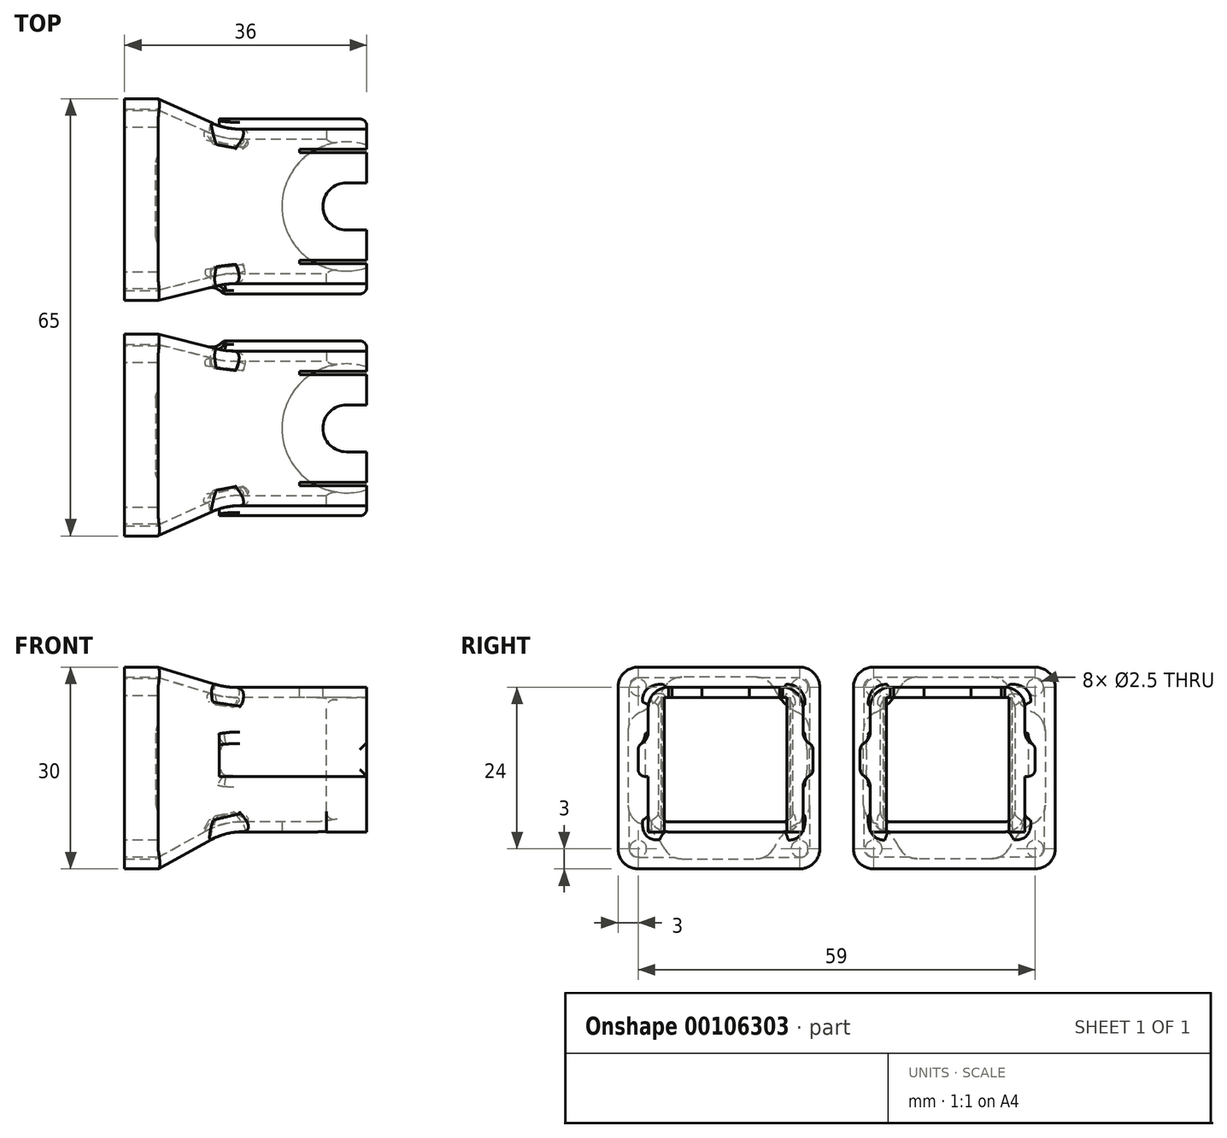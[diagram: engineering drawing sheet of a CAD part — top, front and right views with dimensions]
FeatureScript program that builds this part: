
annotation { "Feature Type Name" : "Feature", "Feature Type Description" : "" }
export const myFeature = defineFeature(function(context is Context, id is Id, definition is map)
    precondition{}
    {
        {
            var Q0;
            Q0=qCreatedBy(makeId("Front.planeOp"),FACE);
            var sketch = newSketch(context, id + "F0", { "sketchPlane" : qUnion([Q0])});
            skLineSegment(sketch, "E0.bottom", {"start": v(10.5, -10.75) * mm, "end": v(-10.5, -10.75) * mm});
            skLineSegment(sketch, "E0.top", {"start": v(10.5, 10.75) * mm, "end": v(-10.5, 10.75) * mm});
            skLineSegment(sketch, "E0.left", {"start": v(10.5, -10.75) * mm, "end": v(10.5, 10.75) * mm});
            skLineSegment(sketch, "E0.right", {"start": v(-10.5, -10.75) * mm, "end": v(-10.5, 10.75) * mm});
            skPoint(sketch, "E0.middle", {"position": v(0, 0) * mm});
            skSolve(sketch);
        }
        {
            var Q0;
            Q0=qSketchRegion(id+"F0",true);
            extrude(context, id + "F1", {"entities" : qUnion([Q0]), "endBound" : BoundingType.SYMMETRIC, "depth" : 23 * mm});
        }
        {
            var Q0;
            Q0=makeQuery(id+"F1.opExtrude","SWEPT_FACE",FACE,{"disambiguationData":[OSD([sQuery(id+"F0.wireOp",EDGE,"E0.right")])]});
            cPlane(context, id + "F2", {"entities" : qUnion([Q0]), "cplaneType" : CPlaneType.OFFSET, "offset" : 10 * mm, "width" : 150 * mm, "height" : 150 * mm});
        }
        {
            var Q0;
            Q0=qCreatedBy(id+"F2.planeOp",FACE);
            var sketch = newSketch(context, id + "F3", { "sketchPlane" : qUnion([Q0])});
            skLineSegment(sketch, "E1.bottom", {"start": v(14, -16.25) * mm, "end": v(-16, -16.25) * mm});
            skLineSegment(sketch, "E1.top", {"start": v(14, 13.75) * mm, "end": v(-16, 13.75) * mm});
            skLineSegment(sketch, "E1.left", {"start": v(14, -16.25) * mm, "end": v(14, 13.75) * mm});
            skLineSegment(sketch, "E1.right", {"start": v(-16, -16.25) * mm, "end": v(-16, 13.75) * mm});
            skPoint(sketch, "E1.middle", {"position": v(-1, -1.25) * mm});
            skSolve(sketch);
        }
        {
            var Q1;
            Q1=makeQuery(id+"F1.opExtrude","SWEPT_FACE",FACE,{"disambiguationData":[OSD([sQuery(id+"F0.wireOp",EDGE,"E0.right")])]});
            var Q2;
            Q2=makeQuery(id+"F3.imprint","IMPRINT",FACE,{"disambiguationData":[TD([[makeQuery(id+"F3.imprint","IMPRINT",EDGE,{"derivedFrom":sQuery(id+"F3.wireOp",EDGE,"E1.bottom")}),-1.0]])]});
            loft(context, id + "F4", {"operationType" : NewBodyOperationType.ADD, "sheetProfilesArray" : [{ "sheetProfileEntities" : qUnion([Q1]) }, { "sheetProfileEntities" : qUnion([Q2]) }]});
        }
        {
            var Q0;
            Q0=makeQuery(id+"F4.opLoft","CAP_FACE",FACE,{"disambiguationData":[OSD([makeQuery(id+"F3.imprint","IMPRINT",FACE,{"disambiguationData":[TD([[makeQuery(id+"F3.imprint","IMPRINT",EDGE,{"derivedFrom":sQuery(id+"F3.wireOp",EDGE,"E1.bottom")}),-1.0]])]})])],"isStart":true});
            var sketch = newSketch(context, id + "F5", { "sketchPlane" : qUnion([Q0])});
            skLineSegment(sketch, "E2.bottom", {"start": v(-16, 13.75) * mm, "end": v(14, 13.75) * mm});
            skLineSegment(sketch, "E2.top", {"start": v(-16, -16.25) * mm, "end": v(14, -16.25) * mm});
            skLineSegment(sketch, "E2.left", {"start": v(-16, 13.75) * mm, "end": v(-16, -16.25) * mm});
            skLineSegment(sketch, "E2.right", {"start": v(14, 13.75) * mm, "end": v(14, -16.25) * mm});
            skSolve(sketch);
        }
        {
            var Q0;
            Q0=qSketchRegion(id+"F5",true);
            extrude(context, id + "F6", {"entities" : qUnion([Q0]), "operationType" : NewBodyOperationType.ADD, "depth" : 5 * mm});
        }
        {
            var Q0;
            {var subQ1=sQuery(id+"F0.wireOp",EDGE,"E0.left");var subQ2=sQuery(id+"F0.wireOp",EDGE,"E0.top");Q0=makeQuery(id+"Fz8CBDRqYWuNpRD_1.boolean.opBoolean","SPLIT",EDGE,{"disambiguationData":[TD([makeQuery(id+"F1.opExtrude","SWEPT_FACE",FACE,{"disambiguationData":[OSD([subQ1])]})])],"derivedFrom":makeQuery(id+"F1.opExtrude","CAP_EDGE",EDGE,{"disambiguationData":[OSD([subQ2])],"isStart":false})});}
            var Q1;
            Q1=makeQuery(id+"F1.opExtrude","CAP_EDGE",EDGE,{"disambiguationData":[OSD([sQuery(id+"F0.wireOp",EDGE,"E0.bottom")])],"isStart":false});
            var Q2;
            {var subQ0=sQuery(id+"F0.wireOp",EDGE,"E0.left");var subQ1=sQuery(id+"F0.wireOp",EDGE,"E0.top");Q2=makeQuery(id+"Fz8CBDRqYWuNpRD_1.boolean.opBoolean","SPLIT",EDGE,{"disambiguationData":[TD([makeQuery(id+"F1.opExtrude","SWEPT_FACE",FACE,{"disambiguationData":[OSD([subQ0])]})])],"derivedFrom":makeQuery(id+"F1.opExtrude","CAP_EDGE",EDGE,{"disambiguationData":[OSD([subQ1])],"isStart":true})});}
            var Q3;
            Q3=makeQuery(id+"F1.opExtrude","CAP_EDGE",EDGE,{"disambiguationData":[OSD([sQuery(id+"F0.wireOp",EDGE,"E0.bottom")])],"isStart":true});
            var Q4;
            Q4=makeQuery(id+"F4.opLoft","SWEPT_EDGE",EDGE,{"disambiguationData":[OSD([sQuery(id+"F0.wireOp",EDGE,"E0.bottom"),sQuery(id+"F0.wireOp",EDGE,"E0.right"),sQuery(id+"F3.wireOp",EDGE,"E1.bottom"),sQuery(id+"F3.wireOp",EDGE,"E1.right")])]});
            var Q5;
            Q5=makeQuery(id+"F4.opLoft","SWEPT_EDGE",EDGE,{"disambiguationData":[OSD([sQuery(id+"F0.wireOp",EDGE,"E0.bottom"),sQuery(id+"F0.wireOp",EDGE,"E0.right"),sQuery(id+"F3.wireOp",EDGE,"E1.bottom"),sQuery(id+"F3.wireOp",EDGE,"E1.left")])]});
            var Q6;
            Q6=makeQuery(id+"F4.opLoft","SWEPT_EDGE",EDGE,{"disambiguationData":[OSD([sQuery(id+"F0.wireOp",EDGE,"E0.top"),sQuery(id+"F0.wireOp",EDGE,"E0.right"),sQuery(id+"F3.wireOp",EDGE,"E1.top"),sQuery(id+"F3.wireOp",EDGE,"E1.left")])]});
            var Q7;
            Q7=makeQuery(id+"F4.opLoft","SWEPT_EDGE",EDGE,{"disambiguationData":[OSD([sQuery(id+"F0.wireOp",EDGE,"E0.top"),sQuery(id+"F0.wireOp",EDGE,"E0.right"),sQuery(id+"F3.wireOp",EDGE,"E1.top"),sQuery(id+"F3.wireOp",EDGE,"E1.right")])]});
            var Q8;
            {var subQ1=sQuery(id+"F0.wireOp",EDGE,"E0.right");var subQ2=sQuery(id+"F0.wireOp",EDGE,"E0.top");Q8=makeQuery(id+"Fz8CBDRqYWuNpRD_1.boolean.opBoolean","SPLIT",EDGE,{"disambiguationData":[TD([makeQuery(id+"F1.opExtrude","SWEPT_FACE",FACE,{"disambiguationData":[OSD([subQ1])]})])],"derivedFrom":makeQuery(id+"F1.opExtrude","CAP_EDGE",EDGE,{"disambiguationData":[OSD([subQ2])],"isStart":false})});}
            var Q9;
            {var subQ1=sQuery(id+"F0.wireOp",EDGE,"E0.right");var subQ2=sQuery(id+"F0.wireOp",EDGE,"E0.top");Q9=makeQuery(id+"Fz8CBDRqYWuNpRD_1.boolean.opBoolean","SPLIT",EDGE,{"disambiguationData":[TD([makeQuery(id+"F1.opExtrude","SWEPT_FACE",FACE,{"disambiguationData":[OSD([subQ1])]})])],"derivedFrom":makeQuery(id+"F1.opExtrude","CAP_EDGE",EDGE,{"disambiguationData":[OSD([subQ2])],"isStart":true})});}
            fillet(context, id + "F7", {"entities" : qUnion([Q0, Q1, Q2, Q3, Q4, Q5, Q6, Q7, Q8, Q9]), "radius" : 3 * mm, "tangentPropagation" : true, "allowEdgeOverflow" : false});
        }
        {
            var Q0;
            {var subQ0=sQuery(id+"F0.wireOp",EDGE,"E0.right");var subQ1=sQuery(id+"F0.wireOp",EDGE,"E0.top");Q0=makeQuery(id+"F4.boolean.opBoolean","MERGE",EDGE,{"derivedFrom":[makeQuery(id+"F1.opExtrude","SWEPT_EDGE",EDGE,{"disambiguationData":[OSD([subQ1,subQ0])]}),makeQuery(id+"F4.opLoft","MID_CAP_EDGE",EDGE,{"disambiguationData":[OSD([subQ1,subQ0])],"capPos":0.0})]});}
            fillet(context, id + "F8", {"entities" : qUnion([Q0]), "radius" : 10 * mm, "tangentPropagation" : true, "allowEdgeOverflow" : false});
        }
        {
            var Q0;
            Q0=makeQuery(id+"F6.opExtrude","CAP_FACE",FACE,{"disambiguationData":[OSD([sQuery(id+"F5.wireOp",EDGE,"E2.bottom"),sQuery(id+"F5.wireOp",EDGE,"E2.top"),sQuery(id+"F5.wireOp",EDGE,"E2.left"),sQuery(id+"F5.wireOp",EDGE,"E2.right")])],"isStart":false});
            var Q1;
            Q1=makeQuery(id+"F7RU65wIXhI5Ua7_1.boolean.opBoolean","COPY",FACE,{"derivedFrom":makeQuery(id+"F7RU65wIXhI5Ua7_1.opExtrude","SWEPT_FACE",FACE,{"disambiguationData":[OSD([sQuery(id+"F3H2WqU3KsAX9Bc_1.wireOp",EDGE,"QCEsvqZN-Nejr-OE69-qjgT-Q3P4DVGDmgon")])]})});
            var Q2;
            Q2=makeQuery(id+"F1.opExtrude","SWEPT_FACE",FACE,{"disambiguationData":[OSD([sQuery(id+"F0.wireOp",EDGE,"E0.left")])]});
            shell(context, id + "F9", {"entities" : qUnion([Q0, Q1, Q2]), "thickness" : 1.5 * mm});
        }
        {
            var Q0;
            Q0=makeQuery(id+"F1.opExtrude","SWEPT_FACE",FACE,{"disambiguationData":[OSD([sQuery(id+"F0.wireOp",EDGE,"E0.top")])]});
            var sketch = newSketch(context, id + "F10", { "sketchPlane" : qUnion([Q0])});
            skLineSegment(sketch, "E3.bottom", {"start": v(4.5, 11.5) * mm, "end": v(10.5, 11.5) * mm});
            skLineSegment(sketch, "E3.top", {"start": v(4.5, 8.5) * mm, "end": v(10.5, 8.5) * mm});
            skLineSegment(sketch, "E3.left", {"start": v(4.5, 11.5) * mm, "end": v(4.5, 8.5) * mm});
            skLineSegment(sketch, "E3.right", {"start": v(10.5, 11.5) * mm, "end": v(10.5, 8.5) * mm});
            skLineSegment(sketch, "E4.MirrorCS", {"start": v(4.5, -11.5) * mm, "end": v(10.5, -11.5) * mm});
            skLineSegment(sketch, "E5.MirrorCS", {"start": v(10.5, -11.5) * mm, "end": v(10.5, -8.5) * mm});
            skLineSegment(sketch, "E6.MirrorCS", {"start": v(4.5, -11.5) * mm, "end": v(4.5, -8.5) * mm});
            skLineSegment(sketch, "E7.MirrorCS", {"start": v(4.5, -8.5) * mm, "end": v(10.5, -8.5) * mm});
            skSolve(sketch);
        }
        {
            var Q0;
            Q0=qSketchRegion(id+"F10",true);
            var Q1;
            Q1=makeQuery(id+"F1.opExtrude","SWEPT_FACE",FACE,{"disambiguationData":[OSD([sQuery(id+"F0.wireOp",EDGE,"E0.bottom")])]});
            extrude(context, id + "F11", {"entities" : qUnion([Q0]), "operationType" : NewBodyOperationType.ADD, "endBound" : BoundingType.UP_TO_SURFACE, "oppositeDirection" : true, "endBoundEntityFace" : qUnion([Q1]), "depth" : 25 * mm});
        }
        {
            var Q0;
            Q0=makeQuery(id+"F11.boolean.opBoolean","MERGE",FACE,{"derivedFrom":[makeQuery(id+"F1.opExtrude","SWEPT_FACE",FACE,{"disambiguationData":[OSD([sQuery(id+"F0.wireOp",EDGE,"E0.top")])]}),makeQuery(id+"F11.opExtrude","CAP_FACE",FACE,{"disambiguationData":[OSD([sQuery(id+"F10.wireOp",EDGE,"E3.bottom"),sQuery(id+"F10.wireOp",EDGE,"E3.top"),sQuery(id+"F10.wireOp",EDGE,"E3.left"),sQuery(id+"F10.wireOp",EDGE,"E3.right")])],"isStart":true}),makeQuery(id+"F11.opExtrude","CAP_FACE",FACE,{"disambiguationData":[OSD([sQuery(id+"F10.wireOp",EDGE,"E4.MirrorCS"),sQuery(id+"F10.wireOp",EDGE,"E5.MirrorCS"),sQuery(id+"F10.wireOp",EDGE,"E6.MirrorCS"),sQuery(id+"F10.wireOp",EDGE,"E7.MirrorCS")])],"isStart":true})]});
            var sketch = newSketch(context, id + "F12", { "sketchPlane" : qUnion([Q0])});
            skArc(sketch, "E8", {"start": v(7.5, 3.5) * mm, "mid": v(4, 0) * mm, "end": v(7.5, -3.5) * mm});
            skLineSegment(sketch, "E9.bottom", {"start": v(7.5, -3.5) * mm, "end": v(10.5, -3.5) * mm});
            skLineSegment(sketch, "E9.top", {"start": v(7.5, 3.5) * mm, "end": v(10.5, 3.5) * mm});
            skLineSegment(sketch, "E9.left", {"start": v(7.5, -3.5) * mm, "end": v(7.5, 3.5) * mm});
            skLineSegment(sketch, "E9.right", {"start": v(10.5, -3.5) * mm, "end": v(10.5, 3.5) * mm});
            skLineSegment(sketch, "E10.bottom", {"start": v(10.5, 8) * mm, "end": v(0.5, 8) * mm});
            skLineSegment(sketch, "E10.top", {"start": v(10.5, 8.5) * mm, "end": v(0.5, 8.5) * mm});
            skLineSegment(sketch, "E10.left", {"start": v(10.5, 8) * mm, "end": v(10.5, 8.5) * mm});
            skLineSegment(sketch, "E10.right", {"start": v(0.5, 8) * mm, "end": v(0.5, 8.5) * mm});
            skLineSegment(sketch, "E11.bottom", {"start": v(10.5, -8) * mm, "end": v(0.5, -8) * mm});
            skLineSegment(sketch, "E11.top", {"start": v(10.5, -8.5) * mm, "end": v(0.5, -8.5) * mm});
            skLineSegment(sketch, "E11.left", {"start": v(10.5, -8) * mm, "end": v(10.5, -8.5) * mm});
            skLineSegment(sketch, "E11.right", {"start": v(0.5, -8) * mm, "end": v(0.5, -8.5) * mm});
            skSolve(sketch);
        }
        {
            var Q0;
            Q0 = qSketchRegion(id + "F12", true);
            extrude(context, id + "F13", {"entities" : qUnion([Q0]), "operationType" : NewBodyOperationType.REMOVE, "endBound" : BoundingType.UP_TO_NEXT, "oppositeDirection" : true, "depth" : 25 * mm});
        }
        {
            var Q0;
            Q0=makeQuery(id+"F6.opExtrude","CAP_FACE",FACE,{"disambiguationData":[OSD([sQuery(id+"F5.wireOp",EDGE,"E2.bottom"),sQuery(id+"F5.wireOp",EDGE,"E2.top"),sQuery(id+"F5.wireOp",EDGE,"E2.left"),sQuery(id+"F5.wireOp",EDGE,"E2.right")])],"isStart":false});
            var sketch = newSketch(context, id + "F14", { "sketchPlane" : qUnion([Q0])});
            skLineSegment(sketch, "E12", {"start": v(11, 10.75) * mm, "end": v(11, -13.25) * mm, "construction": true});
            skLineSegment(sketch, "E13", {"start": v(11, -13.25) * mm, "end": v(-13, -13.25) * mm, "construction": true});
            skCircle(sketch, "E14", {"center": v(11, 10.75) * mm, "radius": 1.25 * mm});
            skCircle(sketch, "E15", {"center": v(11, -13.25) * mm, "radius": 1.25 * mm});
            skCircle(sketch, "E16", {"center": v(-13, -13.25) * mm, "radius": 1.25 * mm});
            skCircle(sketch, "E17", {"center": v(-13, 10.75) * mm, "radius": 1.25 * mm});
            skArc(sketch, "E18", {"start": v(-16, 6.25) * mm, "mid": v(-10.7, 8.45) * mm, "end": v(-8.5, 13.75) * mm});
            skArc(sketch, "E19", {"start": v(6.5, 13.75) * mm, "mid": v(8.7, 8.45) * mm, "end": v(14, 6.25) * mm});
            skArc(sketch, "E20", {"start": v(14, -8.75) * mm, "mid": v(8.7, -10.95) * mm, "end": v(6.5, -16.25) * mm});
            skArc(sketch, "E21", {"start": v(-8.5, -16.25) * mm, "mid": v(-10.7, -10.95) * mm, "end": v(-16, -8.75) * mm});
            skLineSegment(sketch, "E22", {"start": v(6.5, 13.75) * mm, "end": v(14, 13.75) * mm});
            skLineSegment(sketch, "E23", {"start": v(14, -8.75) * mm, "end": v(14, -16.25) * mm});
            skLineSegment(sketch, "E24", {"start": v(-16, 6.25) * mm, "end": v(-16, 13.75) * mm});
            skLineSegment(sketch, "E25", {"start": v(-16, 13.75) * mm, "end": v(-8.5, 13.75) * mm});
            skLineSegment(sketch, "E26", {"start": v(14, 13.75) * mm, "end": v(14, 6.25) * mm});
            skLineSegment(sketch, "E27", {"start": v(14, -16.25) * mm, "end": v(6.5, -16.25) * mm});
            skLineSegment(sketch, "E28", {"start": v(-8.5, -16.25) * mm, "end": v(-16, -16.25) * mm});
            skLineSegment(sketch, "E29", {"start": v(-16, -16.25) * mm, "end": v(-16, -8.75) * mm});
            skSolve(sketch);
        }
        {
            var Q0;
            Q0=qSketchRegion(id+"F14",true);
            var Q1;
            Q1=makeQuery(id+"F1.opExtrude","SWEPT_BODY",BODY,{"disambiguationData":[OSD([sQuery(id+"F0.wireOp",EDGE,"E0.bottom"),sQuery(id+"F0.wireOp",EDGE,"E0.top"),sQuery(id+"F0.wireOp",EDGE,"E0.left"),sQuery(id+"F0.wireOp",EDGE,"E0.right")])]});
            extrude(context, id + "F15", {"entities" : qUnion([Q0]), "operationType" : NewBodyOperationType.ADD, "oppositeDirection" : true, "endBoundEntityBody" : qUnion([Q1]), "depth" : 5 * mm});
        }
        {
            var Q0;
            {var subQ0=sQuery(id+"F0.wireOp",EDGE,"E0.bottom");Q0=makeQuery(id+"F11.boolean.opBoolean","MERGE",FACE,{"derivedFrom":[makeQuery(id+"F1.opExtrude","SWEPT_FACE",FACE,{"disambiguationData":[OSD([subQ0])]}),makeQuery(id+"F11.opExtrude","CAP_FACE",FACE,{"disambiguationData":[OSD([subQ0]),ownerDisambiguation([makeQuery(id+"F11.opExtrude","SWEPT_BODY",BODY,{"disambiguationData":[OSD([sQuery(id+"F10.wireOp",EDGE,"E3.bottom"),sQuery(id+"F10.wireOp",EDGE,"E3.top"),sQuery(id+"F10.wireOp",EDGE,"E3.left"),sQuery(id+"F10.wireOp",EDGE,"E3.right")])]})])],"isStart":false}),makeQuery(id+"F11.opExtrude","CAP_FACE",FACE,{"disambiguationData":[OSD([subQ0]),ownerDisambiguation([makeQuery(id+"F11.opExtrude","SWEPT_BODY",BODY,{"disambiguationData":[OSD([sQuery(id+"F10.wireOp",EDGE,"E4.MirrorCS"),sQuery(id+"F10.wireOp",EDGE,"E5.MirrorCS"),sQuery(id+"F10.wireOp",EDGE,"E6.MirrorCS"),sQuery(id+"F10.wireOp",EDGE,"E7.MirrorCS")])]})])],"isStart":false})]});}
            var sketch = newSketch(context, id + "F16", { "sketchPlane" : qUnion([Q0])});
            skCircle(sketch, "E30", {"center": v(7.5, 0) * mm, "radius": 9.6 * mm});
            skSolve(sketch);
        }
        {
            var Q0;
            Q0=qSketchRegion(id+"F16",true);
            var Q1;
            {var subQ0=sQuery(id+"F0.wireOp",EDGE,"E0.top");Q1=makeQuery(id+"F9.opShell","OFFSET_FACE",FACE,{"disambiguationData":[OSD([subQ0]),TDD([makeQuery(id+"F1.opExtrude","SWEPT_FACE",FACE,{"disambiguationData":[OSD([subQ0])]})])]});}
            extrude(context, id + "F17", {"entities" : qUnion([Q0]), "operationType" : NewBodyOperationType.REMOVE, "endBound" : BoundingType.UP_TO_SURFACE, "oppositeDirection" : true, "endBoundEntityFace" : qUnion([Q1]), "depth" : 25 * mm});
        }
        {
            var Q0;
            Q0=makeQuery(id+"F15.boolean.opBoolean","MERGE",EDGE,{"derivedFrom":[makeQuery(id+"F6.opExtrude","SWEPT_EDGE",EDGE,{"disambiguationData":[OSD([sQuery(id+"F5.wireOp",EDGE,"E2.top"),sQuery(id+"F5.wireOp",EDGE,"E2.left")])]}),makeQuery(id+"F15.opExtrude","SWEPT_EDGE",EDGE,{"disambiguationData":[OSD([sQuery(id+"F14.wireOp",EDGE,"E28"),sQuery(id+"F14.wireOp",EDGE,"E29")])]})]});
            var Q1;
            Q1=makeQuery(id+"F15.boolean.opBoolean","MERGE",EDGE,{"derivedFrom":[makeQuery(id+"F6.opExtrude","SWEPT_EDGE",EDGE,{"disambiguationData":[OSD([sQuery(id+"F5.wireOp",EDGE,"E2.bottom"),sQuery(id+"F5.wireOp",EDGE,"E2.left")])]}),makeQuery(id+"F15.opExtrude","SWEPT_EDGE",EDGE,{"disambiguationData":[OSD([sQuery(id+"F14.wireOp",EDGE,"E24"),sQuery(id+"F14.wireOp",EDGE,"E25")])]})]});
            var Q2;
            Q2=makeQuery(id+"F15.boolean.opBoolean","MERGE",EDGE,{"derivedFrom":[makeQuery(id+"F6.opExtrude","SWEPT_EDGE",EDGE,{"disambiguationData":[OSD([sQuery(id+"F5.wireOp",EDGE,"E2.top"),sQuery(id+"F5.wireOp",EDGE,"E2.right")])]}),makeQuery(id+"F15.opExtrude","SWEPT_EDGE",EDGE,{"disambiguationData":[OSD([sQuery(id+"F14.wireOp",EDGE,"E23"),sQuery(id+"F14.wireOp",EDGE,"E27")])]})]});
            var Q3;
            Q3=makeQuery(id+"F15.boolean.opBoolean","MERGE",EDGE,{"derivedFrom":[makeQuery(id+"F6.opExtrude","SWEPT_EDGE",EDGE,{"disambiguationData":[OSD([sQuery(id+"F5.wireOp",EDGE,"E2.bottom"),sQuery(id+"F5.wireOp",EDGE,"E2.right")])]}),makeQuery(id+"F15.opExtrude","SWEPT_EDGE",EDGE,{"disambiguationData":[OSD([sQuery(id+"F14.wireOp",EDGE,"E22"),sQuery(id+"F14.wireOp",EDGE,"E26")])]})]});
            fillet(context, id + "F18", {"entities" : qUnion([Q0, Q1, Q2, Q3]), "radius" : 3 * mm, "tangentPropagation" : true, "allowEdgeOverflow" : false});
        }
        {
            var Q0;
            Q0=makeQuery(id+"F15.boolean.opBoolean","INTERSECT",EDGE,{"derivedFrom":[makeQuery(id+"F9.opShell","OFFSET_FACE",FACE,{"disambiguationData":[OSD([sQuery(id+"F5.wireOp",EDGE,"E2.left")])]}),makeQuery(id+"F15.opExtrude","SWEPT_FACE",FACE,{"disambiguationData":[OSD([sQuery(id+"F14.wireOp",EDGE,"E18")])]})]});
            var Q1;
            Q1=makeQuery(id+"F15.boolean.opBoolean","INTERSECT",EDGE,{"derivedFrom":[makeQuery(id+"F9.opShell","OFFSET_FACE",FACE,{"disambiguationData":[OSD([sQuery(id+"F5.wireOp",EDGE,"E2.bottom")])]}),makeQuery(id+"F15.opExtrude","SWEPT_FACE",FACE,{"disambiguationData":[OSD([sQuery(id+"F14.wireOp",EDGE,"E18")])]})]});
            var Q2;
            Q2=makeQuery(id+"F15.boolean.opBoolean","INTERSECT",EDGE,{"derivedFrom":[makeQuery(id+"F9.opShell","OFFSET_FACE",FACE,{"disambiguationData":[OSD([sQuery(id+"F5.wireOp",EDGE,"E2.bottom")])]}),makeQuery(id+"F15.opExtrude","SWEPT_FACE",FACE,{"disambiguationData":[OSD([sQuery(id+"F14.wireOp",EDGE,"E19")])]})]});
            var Q3;
            Q3=makeQuery(id+"F15.boolean.opBoolean","INTERSECT",EDGE,{"derivedFrom":[makeQuery(id+"F9.opShell","OFFSET_FACE",FACE,{"disambiguationData":[OSD([sQuery(id+"F5.wireOp",EDGE,"E2.right")])]}),makeQuery(id+"F15.opExtrude","SWEPT_FACE",FACE,{"disambiguationData":[OSD([sQuery(id+"F14.wireOp",EDGE,"E19")])]})]});
            var Q4;
            Q4=makeQuery(id+"F15.boolean.opBoolean","INTERSECT",EDGE,{"derivedFrom":[makeQuery(id+"F9.opShell","OFFSET_FACE",FACE,{"disambiguationData":[OSD([sQuery(id+"F5.wireOp",EDGE,"E2.right")])]}),makeQuery(id+"F15.opExtrude","SWEPT_FACE",FACE,{"disambiguationData":[OSD([sQuery(id+"F14.wireOp",EDGE,"E20")])]})]});
            var Q5;
            Q5=makeQuery(id+"F15.boolean.opBoolean","INTERSECT",EDGE,{"derivedFrom":[makeQuery(id+"F9.opShell","OFFSET_FACE",FACE,{"disambiguationData":[OSD([sQuery(id+"F5.wireOp",EDGE,"E2.top")])]}),makeQuery(id+"F15.opExtrude","SWEPT_FACE",FACE,{"disambiguationData":[OSD([sQuery(id+"F14.wireOp",EDGE,"E20")])]})]});
            var Q6;
            Q6=makeQuery(id+"F15.boolean.opBoolean","INTERSECT",EDGE,{"derivedFrom":[makeQuery(id+"F9.opShell","OFFSET_FACE",FACE,{"disambiguationData":[OSD([sQuery(id+"F5.wireOp",EDGE,"E2.top")])]}),makeQuery(id+"F15.opExtrude","SWEPT_FACE",FACE,{"disambiguationData":[OSD([sQuery(id+"F14.wireOp",EDGE,"E21")])]})]});
            var Q7;
            Q7=makeQuery(id+"F15.boolean.opBoolean","INTERSECT",EDGE,{"derivedFrom":[makeQuery(id+"F9.opShell","OFFSET_FACE",FACE,{"disambiguationData":[OSD([sQuery(id+"F5.wireOp",EDGE,"E2.left")])]}),makeQuery(id+"F15.opExtrude","SWEPT_FACE",FACE,{"disambiguationData":[OSD([sQuery(id+"F14.wireOp",EDGE,"E21")])]})]});
            fillet(context, id + "F19", {"entities" : qUnion([Q0, Q1, Q2, Q3, Q4, Q5, Q6, Q7]), "radius" : 3 * mm, "tangentPropagation" : true, "allowEdgeOverflow" : false});
        }
        {
            var Q0;
            Q0=makeQuery(id+"F17.boolean.opBoolean","INTERSECT",EDGE,{"derivedFrom":[makeQuery(id+"F11.boolean.opBoolean","SPLIT",FACE,{"disambiguationData":[TD([makeQuery(id+"F11.opExtrude","SWEPT_FACE",FACE,{"disambiguationData":[OSD([sQuery(id+"F10.wireOp",EDGE,"E7.MirrorCS")])]})])],"derivedFrom":makeQuery(id+"F11.opExtrude","SWEPT_FACE",FACE,{"disambiguationData":[OSD([sQuery(id+"F10.wireOp",EDGE,"E6.MirrorCS")])]})}),makeQuery(id+"F17.opExtrude","SWEPT_FACE",FACE,{"disambiguationData":[OSD([sQuery(id+"F16.wireOp",EDGE,"E30")])]})]});
            var Q1;
            Q1=makeQuery(id+"F17.boolean.opBoolean","INTERSECT",EDGE,{"derivedFrom":[makeQuery(id+"F11.boolean.opBoolean","SPLIT",FACE,{"disambiguationData":[TD([makeQuery(id+"F11.opExtrude","SWEPT_FACE",FACE,{"disambiguationData":[OSD([sQuery(id+"F10.wireOp",EDGE,"E3.top")])]})])],"derivedFrom":makeQuery(id+"F11.opExtrude","SWEPT_FACE",FACE,{"disambiguationData":[OSD([sQuery(id+"F10.wireOp",EDGE,"E3.left")])]})}),makeQuery(id+"F17.opExtrude","SWEPT_FACE",FACE,{"disambiguationData":[OSD([sQuery(id+"F16.wireOp",EDGE,"E30")])]})]});
            fillet(context, id + "F20", {"entities" : qUnion([Q0, Q1]), "radius" : 2 * mm, "tangentPropagation" : true, "allowEdgeOverflow" : false});
        }
        {
            var Q0;
            Q0=makeQuery(id+"F11.opExtrude","CAP_EDGE",EDGE,{"disambiguationData":[OSD([sQuery(id+"F10.wireOp",EDGE,"E4.MirrorCS")])],"isStart":true});
            var Q1;
            Q1=makeQuery(id+"F11.opExtrude","TWEAK_EDGE",EDGE,{"derivedFrom":[makeQuery(id+"F1.opExtrude","SWEPT_FACE",FACE,{"disambiguationData":[OSD([sQuery(id+"F0.wireOp",EDGE,"E0.bottom")])]}),makeQuery(id+"F10.imprint","IMPRINT",EDGE,{"derivedFrom":sQuery(id+"F10.wireOp",EDGE,"E4.MirrorCS")})]});
            var Q2;
            Q2=makeQuery(id+"F11.opExtrude","TWEAK_EDGE",EDGE,{"derivedFrom":[makeQuery(id+"F1.opExtrude","SWEPT_FACE",FACE,{"disambiguationData":[OSD([sQuery(id+"F0.wireOp",EDGE,"E0.bottom")])]}),makeQuery(id+"F10.imprint","IMPRINT",EDGE,{"derivedFrom":sQuery(id+"F10.wireOp",EDGE,"E3.bottom")})]});
            var Q3;
            Q3=makeQuery(id+"F11.opExtrude","CAP_EDGE",EDGE,{"disambiguationData":[OSD([sQuery(id+"F10.wireOp",EDGE,"E3.bottom")])],"isStart":true});
            fillet(context, id + "F21", {"entities" : qUnion([Q0, Q1, Q2, Q3]), "radius" : 3 * mm, "tangentPropagation" : true, "allowEdgeOverflow" : false});
        }
        {
            var Q0;
            Q0=makeQuery(id+"F11.boolean.opBoolean","MERGE",FACE,{"derivedFrom":[makeQuery(id+"F1.opExtrude","CAP_FACE",FACE,{"disambiguationData":[OSD([sQuery(id+"F0.wireOp",EDGE,"E0.bottom"),sQuery(id+"F0.wireOp",EDGE,"E0.top"),sQuery(id+"F0.wireOp",EDGE,"E0.left"),sQuery(id+"F0.wireOp",EDGE,"E0.right")])],"isStart":true}),makeQuery(id+"F11.opExtrude","SWEPT_FACE",FACE,{"disambiguationData":[OSD([sQuery(id+"F10.wireOp",EDGE,"E3.bottom")])]})]});
            var sketch = newSketch(context, id + "F22", { "sketchPlane" : qUnion([Q0])});
            skLineSegment(sketch, "E31.bottom", {"start": v(11.4, -2.5) * mm, "end": v(-10.5, -2.5) * mm});
            skLineSegment(sketch, "E31.top", {"start": v(11.4, 2.5) * mm, "end": v(-10.5, 2.5) * mm});
            skLineSegment(sketch, "E31.left", {"start": v(11.4, -2.5) * mm, "end": v(11.4, 2.5) * mm});
            skLineSegment(sketch, "E31.right", {"start": v(-10.5, -2.5) * mm, "end": v(-10.5, 2.5) * mm});
            skPoint(sketch, "E31.middle", {"position": v(0.45, 0) * mm});
            skSolve(sketch);
        }
        {
            var Q0;
            Q0=qSketchRegion(id+"F22",true);
            extrude(context, id + "F23", {"entities" : qUnion([Q0]), "depth" : 1.5 * mm});
        }
        {
            var Q0;
            Q0=makeQuery(id+"F23.opExtrude","CAP_EDGE",EDGE,{"disambiguationData":[OSD([sQuery(id+"F22.wireOp",EDGE,"E31.bottom")])],"isStart":false});
            var Q1;
            Q1=makeQuery(id+"F23.opExtrude","CAP_EDGE",EDGE,{"disambiguationData":[OSD([sQuery(id+"F22.wireOp",EDGE,"E31.top")])],"isStart":false});
            var Q2;
            Q2=makeQuery(id+"F23.opExtrude","CAP_EDGE",EDGE,{"disambiguationData":[OSD([sQuery(id+"F22.wireOp",EDGE,"E31.right")])],"isStart":false});
            fillet(context, id + "F24", {"entities" : qUnion([Q0, Q1, Q2]), "radius" : 1 * mm, "tangentPropagation" : true, "allowEdgeOverflow" : false});
        }
        {
            var Q0;
            Q0=makeQuery(id+"F23.opExtrude","SWEPT_BODY",BODY,{"disambiguationData":[OSD([sQuery(id+"F22.wireOp",EDGE,"E31.bottom"),sQuery(id+"F22.wireOp",EDGE,"E31.top"),sQuery(id+"F22.wireOp",EDGE,"E31.left"),sQuery(id+"F22.wireOp",EDGE,"E31.right")])]});
            var Q1;
            Q1=qCreatedBy(makeId("Front.planeOp"),FACE);
            mirror(context, id + "F25", {"operationType" : NewBodyOperationType.ADD, "entities" : qUnion([Q0]), "mirrorPlane" : qUnion([Q1])});
        }
        {
            var Q0;
            Q0=makeQuery(id+"F25.opPattern","COPY",EDGE,{"derivedFrom":makeQuery(id+"F24.opFillet","BLEND_EDGE",EDGE,{"blendedFrom":[makeQuery(id+"F23.opExtrude","CAP_EDGE",EDGE,{"disambiguationData":[OSD([sQuery(id+"F22.wireOp",EDGE,"E31.top")])],"isStart":false}),makeQuery(id+"F23.opExtrude","SWEPT_FACE",FACE,{"disambiguationData":[OSD([sQuery(id+"F22.wireOp",EDGE,"E31.left")])]})],"blendedInto":[makeQuery(id+"F23.opExtrude","SWEPT_FACE",FACE,{"disambiguationData":[OSD([sQuery(id+"F22.wireOp",EDGE,"E31.left")])]})]}),"instanceName":"1"});
            fillet(context, id + "F26", {"entities" : qUnion([Q0]), "radius" : 1 * mm, "tangentPropagation" : true, "allowEdgeOverflow" : false});
        }
        {
            var Q0;
            Q0=makeQuery(id+"F23.opExtrude","CAP_EDGE",EDGE,{"disambiguationData":[OSD([sQuery(id+"F22.wireOp",EDGE,"E31.top")])],"isStart":true});
            var Q1;
            Q1=makeQuery(id+"F25.opPattern","COPY",EDGE,{"derivedFrom":makeQuery(id+"F23.opExtrude","CAP_EDGE",EDGE,{"disambiguationData":[OSD([sQuery(id+"F22.wireOp",EDGE,"E31.top")])],"isStart":true}),"instanceName":"1"});
            var Q2;
            Q2=makeQuery(id+"F25.opPattern","COPY",EDGE,{"derivedFrom":makeQuery(id+"F23.opExtrude","CAP_EDGE",EDGE,{"disambiguationData":[OSD([sQuery(id+"F22.wireOp",EDGE,"E31.bottom")])],"isStart":true}),"instanceName":"1"});
            var Q3;
            Q3=makeQuery(id+"F23.opExtrude","CAP_EDGE",EDGE,{"disambiguationData":[OSD([sQuery(id+"F22.wireOp",EDGE,"E31.bottom")])],"isStart":true});
            fillet(context, id + "F27", {"entities" : qUnion([Q0, Q1, Q2, Q3]), "radius" : 2 * mm, "tangentPropagation" : true, "allowEdgeOverflow" : false});
        }
        {
            var Q0;
            Q0=makeQuery(id+"F1.opExtrude","SWEPT_BODY",BODY,{"disambiguationData":[OSD([sQuery(id+"F0.wireOp",EDGE,"E0.bottom"),sQuery(id+"F0.wireOp",EDGE,"E0.top"),sQuery(id+"F0.wireOp",EDGE,"E0.left"),sQuery(id+"F0.wireOp",EDGE,"E0.right")])]});
            var Q1;
            Q1=makeQuery(id+"F6.opExtrude","SWEPT_FACE",FACE,{"disambiguationData":[OSD([sQuery(id+"F5.wireOp",EDGE,"E2.right")])]});
            mirror(context, id + "F28", {"entities" : qUnion([Q0]), "mirrorPlane" : qUnion([Q1])});
        }
        {
            var Q0;
            Q0=makeQuery(id+"F28.opPattern","COPY",BODY,{"derivedFrom":makeQuery(id+"F1.opExtrude","SWEPT_BODY",BODY,{"disambiguationData":[OSD([sQuery(id+"F0.wireOp",EDGE,"E0.bottom"),sQuery(id+"F0.wireOp",EDGE,"E0.top"),sQuery(id+"F0.wireOp",EDGE,"E0.left"),sQuery(id+"F0.wireOp",EDGE,"E0.right")])]}),"instanceName":"1"});
            var Q1;
            Q1=qCreatedBy(makeId("Front.planeOp"),FACE);
            transform(context, id + "F29", {"entities" : qUnion([Q0]), "transformType" : TransformType.TRANSLATION_DISTANCE, "transformDirection" : qUnion([Q1]), "distance" : 5 * mm, "makeCopy" : false});
        }
    });
